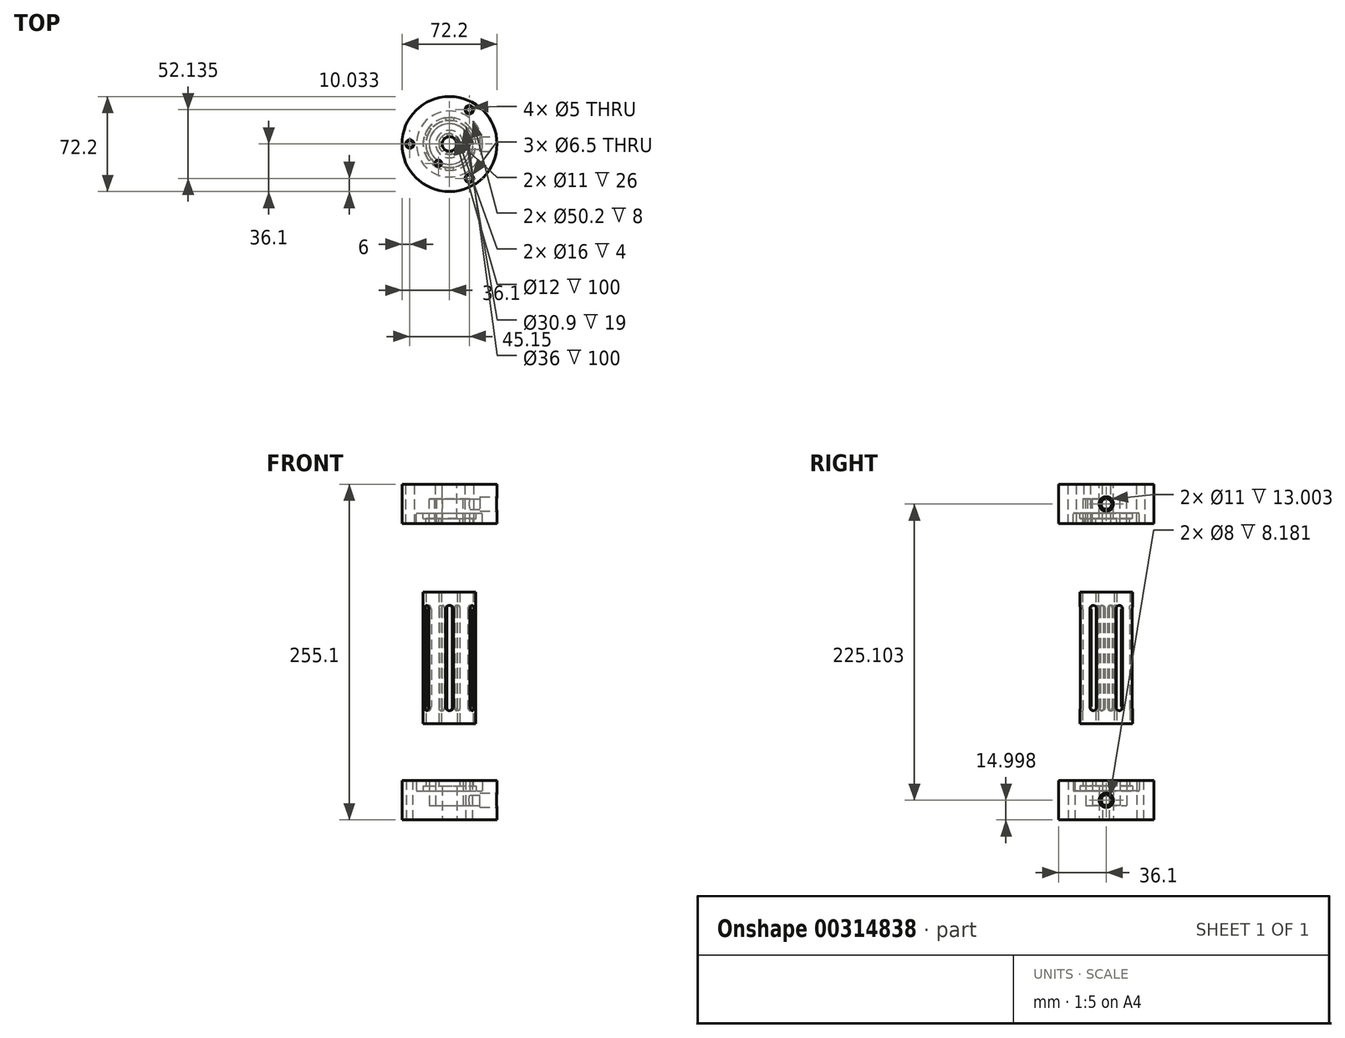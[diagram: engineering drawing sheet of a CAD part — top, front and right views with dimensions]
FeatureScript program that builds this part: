
annotation { "Feature Type Name" : "Feature", "Feature Type Description" : "" }
export const myFeature = defineFeature(function(context is Context, id is Id, definition is map)
    precondition{}
    {
        {
            var Q0;
            Q0=qCreatedBy(makeId("Front.planeOp"),FACE);
            var sketch = newSketch(context, id + "F0", { "sketchPlane" : qUnion([Q0])});
            skLineSegment(sketch, "E0", {"start": v(0, -58.51) * mm, "end": v(0, 53.46) * mm, "construction": true});
            skLineSegment(sketch, "E1.bottom", {"start": v(18, 45.53) * mm, "end": v(20, 45.53) * mm});
            skLineSegment(sketch, "E1.top", {"start": v(18, -54.47) * mm, "end": v(20, -54.47) * mm});
            skLineSegment(sketch, "E1.left", {"start": v(18, 45.53) * mm, "end": v(18, -54.47) * mm});
            skLineSegment(sketch, "E1.right", {"start": v(20, 45.53) * mm, "end": v(20, -54.47) * mm});
            skLineSegment(sketch, "E2.bottom", {"start": v(6, 45.53) * mm, "end": v(8, 45.53) * mm});
            skLineSegment(sketch, "E2.top", {"start": v(6, -54.47) * mm, "end": v(8, -54.47) * mm});
            skLineSegment(sketch, "E2.left", {"start": v(6, 45.53) * mm, "end": v(6, -54.47) * mm});
            skLineSegment(sketch, "E2.right", {"start": v(8, 45.53) * mm, "end": v(8, -54.47) * mm});
            skSolve(sketch);
        }
        {
            var Q0;
            Q0 = qSketchRegion(id + "F0", true);
            var Q1;
            Q1=sQuery(id+"F0.wireOp",EDGE,"E0");
            revolve(context, id + "F1", {"entities" : qUnion([Q0]), "axis" : qUnion([Q1]), "revolveType" : RevolveType.ONE_DIRECTION, "angle" : 60 * degree});
        }
        {
            var Q0;
            Q0=makeQuery(id+"F1.opRevolve","CAP_VERTEX",VERTEX,{"disambiguationData":[OSD([sQuery(id+"F0.wireOp",EDGE,"E1.bottom"),sQuery(id+"F0.wireOp",EDGE,"E1.left")])],"isStart":false});
            var Q1;
            Q1=makeQuery(id+"F1.opRevolve","CAP_VERTEX",VERTEX,{"disambiguationData":[OSD([sQuery(id+"F0.wireOp",EDGE,"E1.bottom"),sQuery(id+"F0.wireOp",EDGE,"E1.left")])],"isStart":true});
            var Q2;
            Q2=makeQuery(id+"F1.opRevolve","CAP_VERTEX",VERTEX,{"disambiguationData":[OSD([sQuery(id+"F0.wireOp",EDGE,"E1.top"),sQuery(id+"F0.wireOp",EDGE,"E1.left")])],"isStart":true});
            cPlane(context, id + "F2", {"entities" : qUnion([Q0, Q1, Q2]), "cplaneType" : CPlaneType.THREE_POINT, "offset" : 25 * mm, "width" : 150 * mm, "height" : 150 * mm});
        }
        {
            var Q0;
            Q0=qCreatedBy(id+"F2.planeOp",FACE);
            var sketch = newSketch(context, id + "F3", { "sketchPlane" : qUnion([Q0])});
            skLineSegment(sketch, "E3.bottom", {"start": v(-9, 45.53) * mm, "end": v(9, 45.53) * mm, "construction": true});
            skLineSegment(sketch, "E3.top", {"start": v(-9, -54.47) * mm, "end": v(9, -54.47) * mm, "construction": true});
            skLineSegment(sketch, "E3.left", {"start": v(-9, 45.53) * mm, "end": v(-9, -54.47) * mm, "construction": true});
            skLineSegment(sketch, "E3.right", {"start": v(9, 45.53) * mm, "end": v(9, -54.47) * mm, "construction": true});
            skPoint(sketch, "E4.startSnap0", {"position": v(0, -54.47) * mm});
            skPoint(sketch, "E4.endSnap0", {"position": v(0, 45.53) * mm});
            skLineSegment(sketch, "E5", {"start": v(9, 45.53) * mm, "end": v(-9, -54.47) * mm, "construction": true});
            skLineSegment(sketch, "E6.bottom", {"start": v(-3, 32.53) * mm, "end": v(3, 32.53) * mm, "construction": true});
            skLineSegment(sketch, "E6.top", {"start": v(-3, -41.47) * mm, "end": v(3, -41.47) * mm, "construction": true});
            skLineSegment(sketch, "E6.left", {"start": v(-3, 32.53) * mm, "end": v(-3, -41.47) * mm});
            skLineSegment(sketch, "E6.right", {"start": v(3, 32.53) * mm, "end": v(3, -41.47) * mm});
            skPoint(sketch, "E6.middle", {"position": v(0, -4.47) * mm});
            skArc(sketch, "E7", {"start": v(3, 32.53) * mm, "mid": v(0, 35.53) * mm, "end": v(-3, 32.53) * mm});
            skArc(sketch, "E8", {"start": v(-3, -41.47) * mm, "mid": v(0, -44.47) * mm, "end": v(3, -41.47) * mm});
            skPoint(sketch, "E9", {"position": v(0, 35.53) * mm});
            skPoint(sketch, "E10", {"position": v(0, -44.47) * mm});
            skSolve(sketch);
        }
        {
            var Q0;
            Q0 = qSketchRegion(id + "F3", true);
            extrude(context, id + "F4", {"entities" : qUnion([Q0]), "operationType" : NewBodyOperationType.REMOVE, "endBound" : BoundingType.THROUGH_ALL, "oppositeDirection" : true, "depth" : 25 * mm});
        }
        {
            var Q0;
            Q0=makeQuery(id+"F1.opRevolve","CAP_VERTEX",VERTEX,{"disambiguationData":[OSD([sQuery(id+"F0.wireOp",EDGE,"E2.bottom"),sQuery(id+"F0.wireOp",EDGE,"E2.left")])],"isStart":false});
            var Q1;
            Q1=makeQuery(id+"F1.opRevolve","CAP_VERTEX",VERTEX,{"disambiguationData":[OSD([sQuery(id+"F0.wireOp",EDGE,"E2.top"),sQuery(id+"F0.wireOp",EDGE,"E2.left")])],"isStart":true});
            var Q2;
            Q2=makeQuery(id+"F1.opRevolve","CAP_VERTEX",VERTEX,{"disambiguationData":[OSD([sQuery(id+"F0.wireOp",EDGE,"E2.bottom"),sQuery(id+"F0.wireOp",EDGE,"E2.left")])],"isStart":true});
            cPlane(context, id + "F5", {"entities" : qUnion([Q0, Q1, Q2]), "cplaneType" : CPlaneType.THREE_POINT, "offset" : 5.8 * mm, "width" : 150 * mm, "height" : 150 * mm});
        }
        {
            var Q0;
            Q0=qCreatedBy(id+"F5.planeOp",FACE);
            var sketch = newSketch(context, id + "F6", { "sketchPlane" : qUnion([Q0])});
            skLineSegment(sketch, "E11", {"start": v(-3, 45.53) * mm, "end": v(3, -54.47) * mm, "construction": true});
            skLineSegment(sketch, "E12.bottom", {"start": v(2, 33.53) * mm, "end": v(-2, 33.53) * mm, "construction": true});
            skLineSegment(sketch, "E12.top", {"start": v(2, -42.47) * mm, "end": v(-2, -42.47) * mm, "construction": true});
            skLineSegment(sketch, "E12.left", {"start": v(2, 33.53) * mm, "end": v(2, -42.47) * mm});
            skLineSegment(sketch, "E12.right", {"start": v(-2, 33.53) * mm, "end": v(-2, -42.47) * mm});
            skPoint(sketch, "E12.middle", {"position": v(0, -4.47) * mm});
            skArc(sketch, "E13", {"start": v(2, 33.53) * mm, "mid": v(0, 35.53) * mm, "end": v(-2, 33.53) * mm});
            skArc(sketch, "E14", {"start": v(-2, -42.47) * mm, "mid": v(0, -44.47) * mm, "end": v(2, -42.47) * mm});
            skPoint(sketch, "E15", {"position": v(0, 35.53) * mm});
            skPoint(sketch, "E16", {"position": v(0, -44.47) * mm});
            skSolve(sketch);
        }
        {
            var Q0;
            Q0 = qSketchRegion(id + "F6", true);
            extrude(context, id + "F7", {"entities" : qUnion([Q0]), "operationType" : NewBodyOperationType.REMOVE, "endBound" : BoundingType.THROUGH_ALL, "depth" : 25 * mm});
        }
        {
            var Q0;
            Q0=makeQuery(id+"F1.opRevolve","SWEPT_BODY",BODY,{"disambiguationData":[OSD([sQuery(id+"F0.wireOp",EDGE,"E1.bottom"),sQuery(id+"F0.wireOp",EDGE,"E1.top"),sQuery(id+"F0.wireOp",EDGE,"E1.left"),sQuery(id+"F0.wireOp",EDGE,"E1.right")])]});
            var Q1;
            Q1=makeQuery(id+"F1.opRevolve","SWEPT_BODY",BODY,{"disambiguationData":[OSD([sQuery(id+"F0.wireOp",EDGE,"E2.bottom"),sQuery(id+"F0.wireOp",EDGE,"E2.top"),sQuery(id+"F0.wireOp",EDGE,"E2.left"),sQuery(id+"F0.wireOp",EDGE,"E2.right")])]});
            var Q2;
            Q2=sQuery(id+"F0.wireOp",EDGE,"E0");
            circularPattern(context, id + "F8", {"operationType" : NewBodyOperationType.ADD, "entities" : qUnion([Q0, Q1]), "axis" : qUnion([Q2]), "angle" : 360 * degree, "instanceCount" : 6, "equalSpace" : true});
        }
        {
            var Q0;
            {var subQ0=makeQuery(id+"F1.opRevolve","SWEPT_FACE",FACE,{"disambiguationData":[OSD([sQuery(id+"F0.wireOp",EDGE,"E2.top")])]});Q0=makeQuery(id+"F8.boolean.opBoolean","MERGE",FACE,{"derivedFrom":[subQ0,makeQuery(id+"F8.opPattern","COPY",FACE,{"derivedFrom":subQ0,"instanceName":"1"}),makeQuery(id+"F8.opPattern","COPY",FACE,{"derivedFrom":subQ0,"instanceName":"2"}),makeQuery(id+"F8.opPattern","COPY",FACE,{"derivedFrom":subQ0,"instanceName":"3"}),makeQuery(id+"F8.opPattern","COPY",FACE,{"derivedFrom":subQ0,"instanceName":"4"}),makeQuery(id+"F8.opPattern","COPY",FACE,{"derivedFrom":subQ0,"instanceName":"5"})]});}
            var sketch = newSketch(context, id + "F9", { "sketchPlane" : qUnion([Q0])});
            skLineSegment(sketch, "E17", {"start": v(6, 0) * mm, "end": v(8, 0) * mm, "construction": true});
            skLineSegment(sketch, "E18", {"start": v(18, 0) * mm, "end": v(20, 0) * mm, "construction": true});
            skPoint(sketch, "E19", {"position": v(7, 0) * mm});
            skPoint(sketch, "E20", {"position": v(19, 0) * mm});
            skSolve(sketch);
        }
        {
            var Q0;
            Q0=qCreatedBy(makeId("Front.planeOp"),FACE);
            var sketch = newSketch(context, id + "F10", { "sketchPlane" : qUnion([Q0])});
            skLineSegment(sketch, "E21", {"start": v(0, -156.44) * mm, "end": v(0, 0) * mm, "construction": true});
            skLineSegment(sketch, "E22", {"start": v(5.5, -101.55) * mm, "end": v(5.5, -127.55) * mm});
            skLineSegment(sketch, "E23", {"start": v(5.5, -127.55) * mm, "end": v(36.1, -127.55) * mm});
            skLineSegment(sketch, "E24", {"start": v(36.1, -127.55) * mm, "end": v(36.1, -97.55) * mm});
            skLineSegment(sketch, "E25", {"start": v(36.1, -97.55) * mm, "end": v(25.1, -97.55) * mm});
            skLineSegment(sketch, "E26", {"start": v(25.1, -97.55) * mm, "end": v(25.1, -105.55) * mm});
            skLineSegment(sketch, "E27", {"start": v(25.1, -105.55) * mm, "end": v(20.1, -105.55) * mm});
            skLineSegment(sketch, "E28", {"start": v(20.1, -105.55) * mm, "end": v(20.1, -101.55) * mm});
            skLineSegment(sketch, "E29", {"start": v(20.1, -101.55) * mm, "end": v(17.9, -101.55) * mm});
            skLineSegment(sketch, "E30", {"start": v(17.9, -101.55) * mm, "end": v(17.9, -97.55) * mm});
            skLineSegment(sketch, "E31", {"start": v(17.9, -97.55) * mm, "end": v(15.45, -97.55) * mm});
            skLineSegment(sketch, "E32", {"start": v(15.45, -97.55) * mm, "end": v(15.45, -116.55) * mm});
            skLineSegment(sketch, "E33", {"start": v(15.45, -116.55) * mm, "end": v(10.45, -116.55) * mm});
            skLineSegment(sketch, "E34", {"start": v(10.45, -116.55) * mm, "end": v(10.45, -97.55) * mm});
            skLineSegment(sketch, "E35", {"start": v(10.45, -97.55) * mm, "end": v(8, -97.55) * mm});
            skLineSegment(sketch, "E36", {"start": v(8, -97.55) * mm, "end": v(8, -101.55) * mm});
            skLineSegment(sketch, "E37", {"start": v(12.95, -116.55) * mm, "end": v(12.95, -74.64) * mm, "construction": true});
            skLineSegment(sketch, "E38", {"start": v(8, -101.55) * mm, "end": v(17.9, -101.55) * mm, "construction": true});
            skPoint(sketch, "E39", {"position": v(12.95, -101.55) * mm});
            skLineSegment(sketch, "E40", {"start": v(15.45, -112.55) * mm, "end": v(36.1, -112.55) * mm, "construction": true});
            skLineSegment(sketch, "E41", {"start": v(19, -54.47) * mm, "end": v(19, -101.55) * mm, "construction": true});
            skLineSegment(sketch, "E42", {"start": v(0, 0) * mm, "end": v(147.93, 0) * mm, "construction": true});
            skLineSegment(sketch, "E43", {"start": v(5.5, -101.55) * mm, "end": v(8, -101.55) * mm});
            skLineSegment(sketch, "E44", {"start": v(8, -97.55) * mm, "end": v(8, -58.57) * mm, "construction": true});
            skSolve(sketch);
        }
        {
            var Q0;
            Q0 = qSketchRegion(id + "F10", true);
            var Q1;
            Q1=sQuery(id+"F10.wireOp",EDGE,"E21");
            revolve(context, id + "F11", {"entities" : qUnion([Q0]), "axis" : qUnion([Q1]), "revolveType" : RevolveType.FULL});
        }
        {
            var Q0;
            Q0=makeQuery(id+"F11.opRevolve","SWEPT_FACE",FACE,{"disambiguationData":[OSD([sQuery(id+"F10.wireOp",EDGE,"E25")])]});
            var sketch = newSketch(context, id + "F12", { "sketchPlane" : qUnion([Q0])});
            skCircle(sketch, "E45", {"center": v(16.9, 0) * mm, "radius": 3 * mm});
            skPoint(sketch, "E46", {"position": v(19.9, 0) * mm});
            skCircle(sketch, "E47", {"center": v(16.9, 0) * mm, "radius": 2.5 * mm});
            skCircle(sketch, "E48", {"center": v(-30.1, 0) * mm, "radius": 2.5 * mm});
            skCircle(sketch, "E49.1.0", {"center": v(15.05, -26.07) * mm, "radius": 2.5 * mm});
            skCircle(sketch, "E49.2.0", {"center": v(15.05, 26.07) * mm, "radius": 2.5 * mm});
            skPoint(sketch, "E49.center", {"position": v(0, 0) * mm});
            skLineSegment(sketch, "E50", {"start": v(36.1, -62.59) * mm, "end": v(36.1, 44.73) * mm, "construction": true});
            skSolve(sketch);
        }
        {
            var Q0;
            Q0=makeQuery(id+"F12.imprint","IMPRINT",FACE,{"disambiguationData":[TD([[makeQuery(id+"F12.imprint","IMPRINT",EDGE,{"derivedFrom":sQuery(id+"F12.wireOp",EDGE,"E48")}),1.0]])]});
            var Q1;
            Q1=makeQuery(id+"F12.imprint","IMPRINT",FACE,{"disambiguationData":[TD([[makeQuery(id+"F12.imprint","IMPRINT",EDGE,{"derivedFrom":sQuery(id+"F12.wireOp",EDGE,"E49.2.0")}),1.0]])]});
            var Q2;
            Q2=makeQuery(id+"F12.imprint","IMPRINT",FACE,{"disambiguationData":[TD([[makeQuery(id+"F12.imprint","IMPRINT",EDGE,{"derivedFrom":sQuery(id+"F12.wireOp",EDGE,"E49.1.0")}),1.0]])]});
            extrude(context, id + "F13", {"entities" : qUnion([Q0, Q1, Q2]), "operationType" : NewBodyOperationType.REMOVE, "endBound" : BoundingType.THROUGH_ALL, "oppositeDirection" : true, "depth" : 25 * mm});
        }
        {
            var Q0;
            Q0=sQuery(id+"F12.wireOp",EDGE,"E50");
            cPlane(context, id + "F14", {"entities" : qUnion([Q0]), "cplaneType" : CPlaneType.LINE_ANGLE, "offset" : 25 * mm, "angle" : 90 * degree, "width" : 150 * mm, "height" : 150 * mm});
        }
        {
            var Q0;
            Q0=qCreatedBy(id+"F14.planeOp",FACE);
            var sketch = newSketch(context, id + "F15", { "sketchPlane" : qUnion([Q0])});
            skCircle(sketch, "E51", {"center": v(0, -112.55) * mm, "radius": 4 * mm});
            skLineSegment(sketch, "E52", {"start": v(-17.53, -116.55) * mm, "end": v(22.72, -116.55) * mm, "construction": true});
            skCircle(sketch, "E53", {"center": v(0, -112.55) * mm, "radius": 5.5 * mm});
            skSolve(sketch);
        }
        {
            var Q0;
            Q0=makeQuery(id+"F15.imprint","IMPRINT",FACE,{"disambiguationData":[TD([[makeQuery(id+"F15.imprint","IMPRINT",EDGE,{"derivedFrom":sQuery(id+"F15.wireOp",EDGE,"E51")}),1.0]])]});
            var Q1;
            Q1=makeQuery(id+"F15.imprint","IMPRINT",FACE,{"disambiguationData":[TD([[makeQuery(id+"F15.imprint","IMPRINT",EDGE,{"derivedFrom":sQuery(id+"F15.wireOp",EDGE,"E51")}),-1.0]])]});
            extrude(context, id + "F16", {"entities" : qUnion([Q0, Q1]), "operationType" : NewBodyOperationType.REMOVE, "oppositeDirection" : true, "depth" : 13 * mm});
        }
        {
            var Q0;
            Q0=makeQuery(id+"F15.imprint","IMPRINT",FACE,{"disambiguationData":[TD([[makeQuery(id+"F15.imprint","IMPRINT",EDGE,{"derivedFrom":sQuery(id+"F15.wireOp",EDGE,"E51")}),1.0]])]});
            var Q1;
            Q1=makeQuery(id+"F11.opRevolve","SWEPT_FACE",FACE,{"disambiguationData":[OSD([sQuery(id+"F10.wireOp",EDGE,"E34")])]});
            extrude(context, id + "F17", {"entities" : qUnion([Q0]), "operationType" : NewBodyOperationType.REMOVE, "endBound" : BoundingType.UP_TO_SURFACE, "oppositeDirection" : true, "endBoundEntityFace" : qUnion([Q1]), "depth" : 25 * mm});
        }
        {
            var Q0;
            Q0=makeQuery(id+"F11.opRevolve","SWEPT_BODY",BODY,{"disambiguationData":[OSD([sQuery(id+"F10.wireOp",EDGE,"E22"),sQuery(id+"F10.wireOp",EDGE,"E23"),sQuery(id+"F10.wireOp",EDGE,"E24"),sQuery(id+"F10.wireOp",EDGE,"E25"),sQuery(id+"F10.wireOp",EDGE,"E26"),sQuery(id+"F10.wireOp",EDGE,"E27"),sQuery(id+"F10.wireOp",EDGE,"E28"),sQuery(id+"F10.wireOp",EDGE,"E29"),sQuery(id+"F10.wireOp",EDGE,"E30"),sQuery(id+"F10.wireOp",EDGE,"E31"),sQuery(id+"F10.wireOp",EDGE,"E32"),sQuery(id+"F10.wireOp",EDGE,"E33"),sQuery(id+"F10.wireOp",EDGE,"E34"),sQuery(id+"F10.wireOp",EDGE,"E35"),sQuery(id+"F10.wireOp",EDGE,"E36"),sQuery(id+"F10.wireOp",EDGE,"JGKVZV8O-XVJ6-IAyT-gw0q-XER2hBgi6qgc"),sQuery(id+"F10.wireOp",EDGE,"EzJfqHeT-wedu-hHKi-CJel-ENcm0yV7M3N1"),sQuery(id+"F10.wireOp",EDGE,"cUD6teWn-UcgJ-km6F-hJ6V-pW2r0hKp5NT0")])]});
            var Q1;
            Q1=qCreatedBy(makeId("Top.planeOp"),FACE);
            mirror(context, id + "F18", {"entities" : qUnion([Q0]), "mirrorPlane" : qUnion([Q1])});
        }
        {
            var Q0;
            Q0=makeQuery(id+"F18.opPattern","COPY",FACE,{"derivedFrom":makeQuery(id+"F11.opRevolve","SWEPT_FACE",FACE,{"disambiguationData":[OSD([sQuery(id+"F10.wireOp",EDGE,"E25")])]}),"instanceName":"1"});
            var sketch = newSketch(context, id + "F19", { "sketchPlane" : qUnion([Q0])});
            skCircle(sketch, "E54", {"center": v(-30.1, 0) * mm, "radius": 3.25 * mm});
            skCircle(sketch, "E55.1.0", {"center": v(15.05, -26.07) * mm, "radius": 3.25 * mm});
            skCircle(sketch, "E55.2.0", {"center": v(15.05, 26.07) * mm, "radius": 3.25 * mm});
            skPoint(sketch, "E55.center", {"position": v(0, 0) * mm});
            skCircle(sketch, "E56", {"center": v(-8.45, 14.64) * mm, "radius": 3 * mm});
            skCircle(sketch, "E57", {"center": v(-8.45, 14.64) * mm, "radius": 2.5 * mm});
            skLineSegment(sketch, "E58", {"start": v(0, 0) * mm, "end": v(-8.45, 14.64) * mm, "construction": true});
            skLineSegment(sketch, "E59", {"start": v(0, 0) * mm, "end": v(15.05, 26.07) * mm, "construction": true});
            skSolve(sketch);
        }
        {
            var Q0;
            Q0=makeQuery(id+"F19.imprint","IMPRINT",FACE,{"disambiguationData":[TD([[makeQuery(id+"F19.imprint","IMPRINT",EDGE,{"derivedFrom":sQuery(id+"F19.wireOp",EDGE,"E55.2.0")}),1.0]])]});
            var Q1;
            Q1=makeQuery(id+"F19.imprint","IMPRINT",FACE,{"disambiguationData":[TD([[makeQuery(id+"F19.imprint","IMPRINT",EDGE,{"derivedFrom":sQuery(id+"F19.wireOp",EDGE,"E57")}),1.0]])]});
            var Q2;
            Q2=makeQuery(id+"F19.imprint","IMPRINT",FACE,{"disambiguationData":[TD([[makeQuery(id+"F19.imprint","IMPRINT",EDGE,{"derivedFrom":sQuery(id+"F19.wireOp",EDGE,"E54")}),1.0]])]});
            var Q3;
            Q3=makeQuery(id+"F19.imprint","IMPRINT",FACE,{"disambiguationData":[TD([[makeQuery(id+"F19.imprint","IMPRINT",EDGE,{"derivedFrom":sQuery(id+"F19.wireOp",EDGE,"E55.1.0")}),1.0]])]});
            extrude(context, id + "F20", {"entities" : qUnion([Q0, Q1, Q2, Q3]), "operationType" : NewBodyOperationType.REMOVE, "endBound" : BoundingType.THROUGH_ALL, "oppositeDirection" : true, "depth" : 25 * mm});
        }
        {
            var Q0;
            Q0=makeQuery(id+"F19.imprint","IMPRINT",FACE,{"disambiguationData":[TD([[makeQuery(id+"F19.imprint","IMPRINT",EDGE,{"derivedFrom":sQuery(id+"F19.wireOp",EDGE,"E56")}),1.0]])]});
            extrude(context, id + "F21", {"entities" : qUnion([Q0]), "operationType" : NewBodyOperationType.REMOVE, "oppositeDirection" : true, "depth" : 19 * mm});
        }
    });
